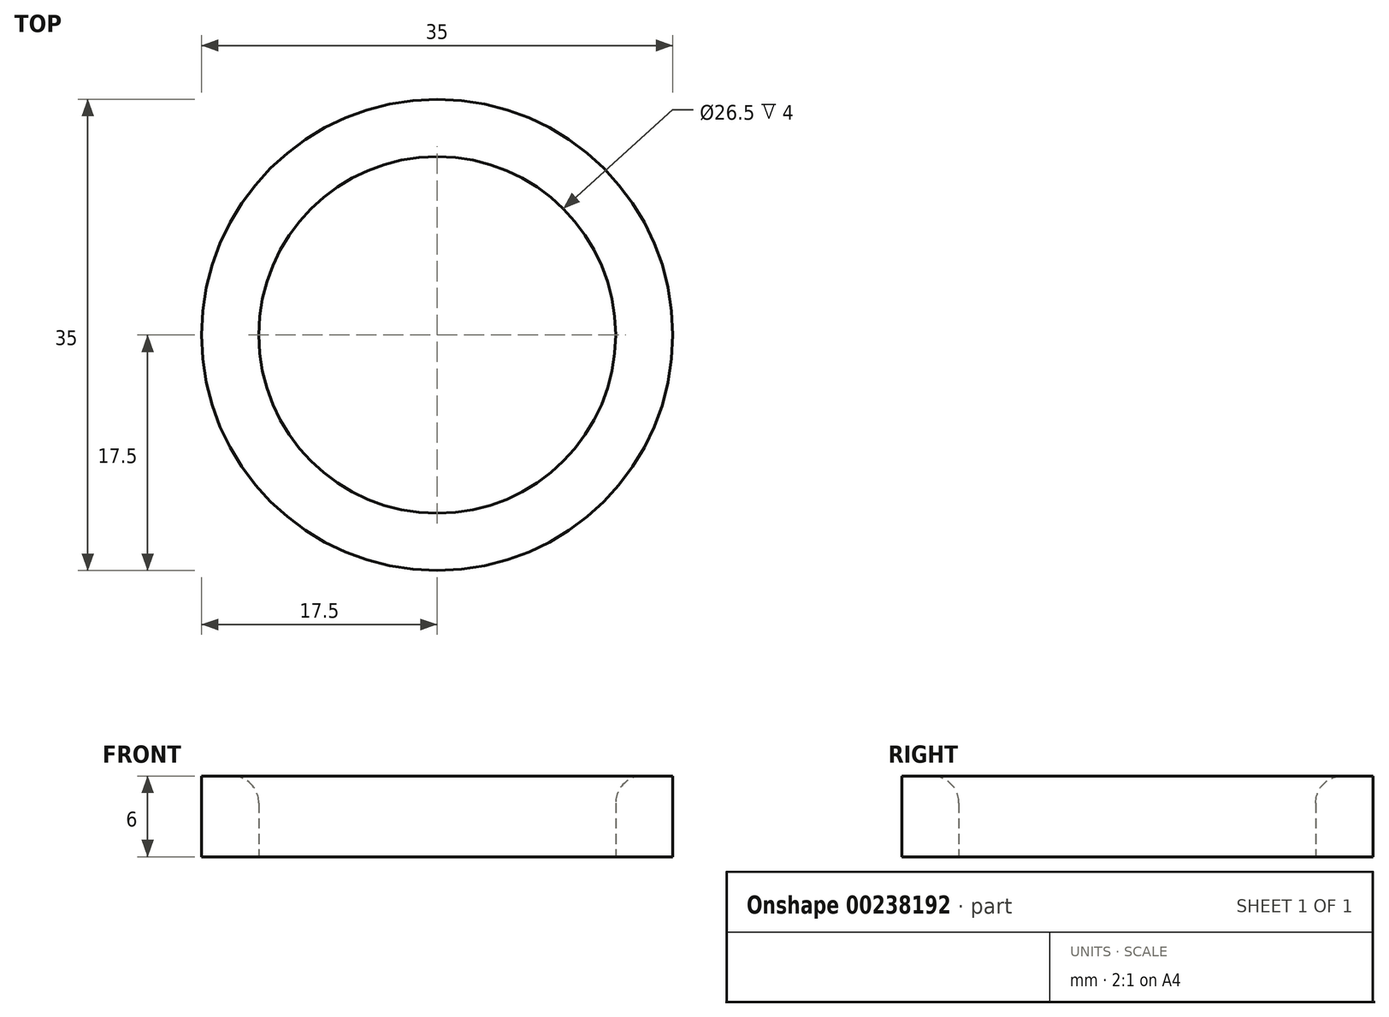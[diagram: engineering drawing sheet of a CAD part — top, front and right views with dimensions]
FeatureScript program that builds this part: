
annotation { "Feature Type Name" : "Feature", "Feature Type Description" : "" }
export const myFeature = defineFeature(function(context is Context, id is Id, definition is map)
    precondition{}
    {
        {
            var Q0;
            Q0=qCreatedBy(makeId("Top.planeOp"),FACE);
            var sketch = newSketch(context, id + "F0", { "sketchPlane" : qUnion([Q0])});
            skCircle(sketch, "E0", {"center": v(0, 0) * mm, "radius": 17.5 * mm});
            skSolve(sketch);
        }
        {
            var Q0;
            Q0 = qSketchRegion(id + "F0", true);
            extrude(context, id + "F1", {"entities" : qUnion([Q0]), "depth" : 6 * mm, "offsetDistance" : 25 * mm});
        }
        {
            var Q0;
            Q0=qCreatedBy(makeId("Top.planeOp"),FACE);
            var sketch = newSketch(context, id + "F2", { "sketchPlane" : qUnion([Q0])});
            skCircle(sketch, "E1", {"center": v(0, 0) * mm, "radius": 13.25 * mm});
            skSolve(sketch);
        }
        {
            var Q0;
            Q0 = qSketchRegion(id + "F2", true);
            extrude(context, id + "F3", {"entities" : qUnion([Q0]), "operationType" : NewBodyOperationType.REMOVE, "depth" : 25 * mm, "offsetDistance" : 25 * mm});
        }
        {
            var Q0;
            Q0=makeQuery(id+"F3.boolean.opBoolean","COPY",EDGE,{"derivedFrom":makeQuery(id+"F3.opExtrude","CAP_EDGE",EDGE,{"disambiguationData":[OSD([sQuery(id+"F2.wireOp",EDGE,"E1")])],"isStart":true})});
            var Q1;
            Q1=makeQuery(id+"F3.boolean.opBoolean","INTERSECT",EDGE,{"derivedFrom":[makeQuery(id+"F1.opExtrude","CAP_FACE",FACE,{"disambiguationData":[OSD([sQuery(id+"F0.wireOp",EDGE,"E0")])],"isStart":false}),makeQuery(id+"F3.opExtrude","SWEPT_FACE",FACE,{"disambiguationData":[OSD([sQuery(id+"F2.wireOp",EDGE,"E1")])]})]});
            fillet(context, id + "F4", {"entities" : qUnion([Q0, Q1]), "radius" : 2 * mm, "tangentPropagation" : true, "allowEdgeOverflow" : false});
        }
    });
